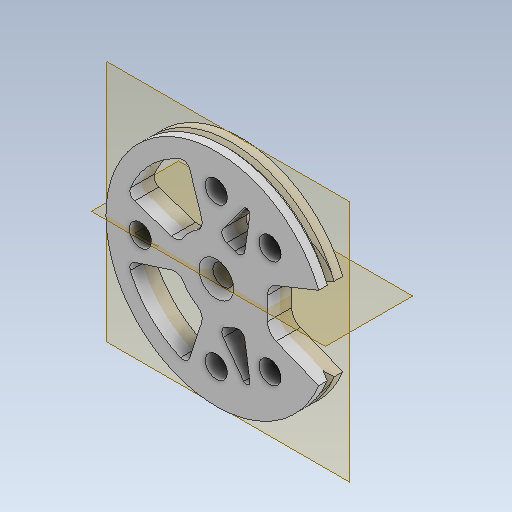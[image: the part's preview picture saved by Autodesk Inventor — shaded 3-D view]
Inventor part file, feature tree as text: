
AUTODESK INVENTOR PART (.ipt)
format: ipt  version: 2020 (Build 240168000, 168)  size: 409,600 bytes
history: native  units: mm
features: sketch x14, extrude x13, projected_geometry x12, other x7, fillet x5, plane x4, reference x4, revolve x1, chamfer x1, mirror x1
ambient origin geometry x8: Origin, YZ Plane, XZ Plane, XY Plane, X Axis, Y Axis, Z Axis, Center Point
bodies: Solid1 (feature_tree)
feature tree (62):
  extrude  "Extrusion1"  Depth=3.5mm TaperAngle=0.0deg
  sketch  "Sketch2"  dims[d3=8.0mm d4=3.5mm d5=0.0mm]
  plane  "Work Plane1"
  extrude  "Extrusion2"  Depth=3.5mm TaperAngle=0.0deg
  extrude  "Extrusion3"  Depth=20.0mm TaperAngle=0.0deg
  plane  "Work Plane2"
  extrude  "Extrusion4"  Depth=10.0mm
  plane  "Work Plane3"
  revolve  "Revolution1"  [1 undecoded]
  extrude  "Extrusion5"  Depth=0.5mm
  extrude  "Extrusion6"  Depth=0.5mm
  fillet  "Fillet1"  Radius=20.0mm
  extrude  "Extrusion7"  TaperAngle=45.0deg  [1 undecoded]
  extrude  "Extrusion8"  Depth=11.0mm
  extrude  "Extrusion9"  Depth=11.0mm
  extrude  "Extrusion10"  Depth=20.0mm TaperAngle=0.0deg
  extrude  "Extrusion11"  Depth=3.839724mm
  extrude  "Extrusion12"  Depth=2.0mm
  fillet  "Fillet2"  Radius=0.7mm
  chamfer  "Chamfer1"  Distance=20.0mm
  extrude  "Extrusion13"  Depth=1.5mm TaperAngle=0.0deg
  fillet  "Fillet3"  Radius=11.0mm
  fillet  "Fillet4"  Radius=3.2mm
  plane  "Work Plane4"
  mirror  "Mirror1"
  fillet  "Fillet5"  Radius=11.0mm
  sketch  "Sketch1"  dims[d0=32.0mm d1=3.5mm d2=0.0mm]
  reference  "Reference1"
  reference  "Reference2"
  reference  "Reference3"
  reference  "Reference4"
  sketch  "Sketch3"  dims[d6=3.0mm d7=20.0mm d8=0.0mm]
  projected_geometry  "Projected Loop1"
  sketch  "Sketch4"  dims[d9=10.0mm d10=3.0mm]
  projected_geometry  "Projected Loop2"
  sketch  "Sketch5"  dims[d11=3.0mm d12=20.0mm d13=0.0mm]
  projected_geometry  "Projected Loop3"
  projected_geometry  "Projected Loop4"
  sketch  "Sketch6"  dims[d14=1.5mm d15=0.5mm]
  projected_geometry  "Projected Loop5"
  sketch  "Sketch7"  dims[d16=0.5mm d17=0.5mm d18=20.0mm]
  projected_geometry  "Projected Loop6"
  sketch  "Sketch8"  dims[d19=90.0deg d20=45.0deg]
  projected_geometry  "Projected Loop7"
  sketch  "Sketch9"  dims[d21=45.0deg d22=11.0mm]
  projected_geometry  "Projected Loop8"
  sketch  "Sketch10"  dims[d23=3.2mm d24=11.0mm]
  sketch  "Sketch11"  dims[d25=3.2mm d26=20.0mm d27=0.0mm]
  projected_geometry  "Projected Loop9"
  sketch  "Sketch12"  dims[d28=3.839724mm d29=3.839724mm]
  projected_geometry  "Projected Loop10"
  sketch  "Sketch13"  dims[d30=20.0mm d31=0.0mm d32=2.0mm d33=0.7mm d34=20.0mm d35=0.0mm]
  projected_geometry  "Projected Loop11"
  sketch  "Sketch14"  dims[d36=0.7mm d37=20.0mm d38=0.0mm d41=11.0mm d42=3.2mm d43=11.0mm d44=3.2mm d45=20.0mm d46=0.0mm d47=20.0mm d48=0.0mm d49=11.0mm d50=3.2mm d51=20.0mm d52=0.0mm d53=27.0mm d54=11.0mm d55=3.141593mm d56=3.141593mm d57=3.141593mm d58=3.141593mm d59=20.0mm d60=0.0mm d61=1.5mm d62=1.0mm d63=1.0mm d64=2.0mm d65=45.0deg d66=11.0mm d67=13.5mm d68=20.0mm d69=0.0mm d70=0.5mm d71=1.0mm d72=1.5mm]
  projected_geometry  "Projected Loop12"
  parser-record x1  (decoder bookkeeping rows leaked as tree rows — omitted from the tree; the rows remain in map.json)
  other  "reducer_1.iam"
  other  "bearing_3_6_2:1"
  other  "tendon_wh_1:1"
  other  "mot_holder_1:1"
  other  "mot_27_ass:1"
  other  "mot_27_1:1"
note: 2 required parameter values undecoded (feature->parameter linkage not recoverable at this tier; creation-order binding heuristic only, values carry confidence <= 0.55)
note: 1 file-system path scrubbed to <path> (originals preserved in map.json)